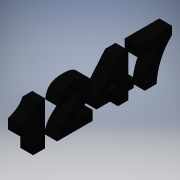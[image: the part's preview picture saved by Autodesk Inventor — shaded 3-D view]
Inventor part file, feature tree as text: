
AUTODESK INVENTOR PART (.ipt)
format: ipt  version: 2016 (Build 200138000, 138)  size: 816,128 bytes
history: native  units: in
note: dims shown in document units (in); Inventor stores cm internally (conversion verified against a paired STEP export)
features: sketch x24, extrude x18, projected_geometry x11, plane x9, loft x4, other x3, mirror x1, emboss x1, fillet x1
ambient origin geometry x8: Origin, YZ Plane, XZ Plane, XY Plane, X Axis, Y Axis, Z Axis, Center Point
bodies: Solid1 (feature_tree)
feature tree (72):
  sketch  "Sketch1"  dims[d0=0.7559in d1=0.7559in]
  plane  "Work Plane1"
  loft  "Loft1"
  extrude  "Extrusion1"  Depth=0.2in
  plane  "Work Plane4"
  loft  "Loft2"
  plane  "Work Plane5"
  loft  "Loft3"
  loft  "Loft4"
  extrude  "Extrusion2"  TaperAngle=0.0deg  [1 undecoded]
  plane  "Work Plane6"
  extrude  "Extrusion3"  Depth=1.0in
  extrude  "Extrusion4"  Depth=1.0651in
  extrude  "Extrusion5"  Depth=0.962in
  plane  "Work Plane7"
  extrude  "Extrusion6"  Depth=0.075in
  plane  "Work Plane8"
  other  "Work Axis1"
  plane  "Work Plane9"
  extrude  "Extrusion7"  Depth=0.06in
  mirror  "Mirror3"
  extrude  "Extrusion8"  Depth=0.05in
  plane  "Work Plane10"
  extrude  "Extrusion9"  Depth=0.0625in
  plane  "Work Plane11"
  extrude  "Extrusion10"  Depth=0.075in
  extrude  "Extrusion11"  TaperAngle=0.0deg  [1 undecoded]
  extrude  "Extrusion12"  Depth=0.2in
  extrude  "Extrusion13"  TaperAngle=0.0deg  [1 undecoded]
  emboss  "Emboss1"
  extrude  "Extrusion16"  Depth=0.01in
  extrude  "Extrusion17"  Depth=0.0344in
  extrude  "Extrusion18"  TaperAngle=60.0deg  [1 undecoded]
  fillet  "Fillet1"  [1 undecoded]
  extrude  "Extrusion19"  Depth=0.05in
  extrude  "Extrusion20"  Depth=0.05in
  sketch  "Sketch2"  dims[d2=0.9963in d3=0.2in]
  sketch  "Sketch3"  dims[d4=0.5in d6=0.08in]
  sketch  "Sketch4"  dims[d7=0.55in d8=150.0deg]
  other  "Edges1"
  sketch  "Sketch5"  dims[d9=150.0deg d14=0.33in]
  projected_geometry  "Projected Loop1"
  other  "Edges2"
  sketch  "Sketch6"  dims[d15=0.66in d18=0.0in d19=90.0deg]
  sketch  "Sketch7"  dims[d20=0.0in d21=90.0deg d22=1.0in]
  sketch  "Sketch8"  dims[d26=1.0651in d28=1.0651in]
  sketch  "Sketch9"  dims[d29=0.0in d30=0.962in]
  sketch  "Sketch10"  dims[d31=0.962in d32=0.075in]
  sketch  "Sketch11"  dims[d33=0.15in d34=0.06in]
  sketch  "Sketch12"  dims[d35=0.1in d36=0.05in]
  sketch  "Sketch13"  dims[d37=0.45in d38=0.0in d39=0.0625in]
  projected_geometry  "Projected Loop2"
  projected_geometry  "Projected Loop3"
  sketch  "Sketch14"  dims[d40=0.01in d41=0.075in]
  projected_geometry  "Projected Loop4"
  sketch  "Sketch15"  dims[d42=0.01in d43=0.0in d44=90.0deg]
  sketch  "Sketch16"  dims[d45=0.0in d46=90.0deg d47=0.2in]
  sketch  "Sketch17"  dims[d48=0.07in d49=0.0in d50=90.0deg]
  sketch  "Sketch18"  dims[d51=0.0in d52=90.0deg d53=0.01in]
  sketch  "Sketch19"  dims[d54=0.01in d55=0.0344in]
  sketch  "Sketch23"  dims[d56=150.0deg d57=60.0deg d58=150.0deg]
  projected_geometry  "Projected Loop6"
  sketch  "Sketch24"  dims[d59=0.7in d60=0.05in]
  sketch  "Sketch25"  dims[d61=0.05in d62=0.05in d63=0.05in]
  sketch  "Sketch26"  dims[d64=0.05in]
  projected_geometry  "Projected Loop7"
  projected_geometry  "Projected Loop8"
  sketch  "Sketch27"  dims[d65=0.01in d66=0.0in d67=90.0deg d68=0.0in d69=90.0deg d70=0.1in d71=0.4in d72=0.15in d73=0.05in d74=0.0in d75=0.02in d77=0.15in d78=0.02in d79=0.1in d80=0.1in d81=0.1in d82=0.02in d83=0.15in d84=0.05in d85=0.0in d86=0.045in d87=0.0in d88=0.025in d89=0.0in d90=0.02in d91=0.02in d92=0.005in d93=0.0in d94=90.0deg d95=0.4466in d96=1.0in d97=0.0in d98=1.0in d99=0.0in d100=0.6528in d101=0.0in d102=0.0in d103=1.0in d104=0.0in d106=90.0deg d107=1.0in d108=0.0in d109=1.65in d110=0.1in d111=0.1in d112=0.0in d113=0.1in d114=0.075in d115=0.0in d116=0.05in d117=0.0in d123=0.84in d124=0.8in d125=0.0in d126=0.0in d127=1.0in d128=0.0in d130=0.15in d131=-0.0206in d135=0.2in d136=0.05in d137=0.1in d138=0.05in d139=0.0in d140=0.025in d141=0.0in]
  projected_geometry  "Projected Loop9"
  projected_geometry  "Projected Loop10"
  projected_geometry  "Projected Loop11"
  projected_geometry  "Projected Loop12"
note: 5 required parameter values undecoded (feature->parameter linkage not recoverable at this tier; creation-order binding heuristic only, values carry confidence <= 0.55)
